# Revit family: EKF_EE_КозырекFORT_PROxima
name_source: partatom
category: Электрооборудование
units: mm (PartAtom-declared; Revit-internal decimal feet)

## family parameters
Всегда вертикально = Нет
На основе рабочей плоскости = Да
Общий = Да
При загрузке вырезать с полостями = Нет
Размер круглого соединителя = Использовать диаметр
Тип детали = Силовой щит
Точка расчета площади = Нет

## types (12) — shared parameters
ADSK_Единица измерения = шт.
ADSK_Завод-изготовитель = EKF
ADSK_Количество = 1
ADSK_Марка = Козырек для FORT
ADSK_Материал = Сталь, с порошковым покрытием, белый
ADSK_Обозначение = Козырек для FORT
ADSK_Размер_Высота = 146 мм
Изготовитель = EKF
Серия номенклатуры = PROxima
Степень защиты IP = -
ТВ = EKF_2
Тип установки = -
zero-valued in all types: ADSK_Масса, Отметка по умолчанию

## per-type parameters (varying)
| type | ADSK_Код изделия | ADSK_Размер_Глубина | ADSK_Размер_Ширина | Тип |
| Козырек для FORT 1000х400 EKF PROxima | FKK104 | 498 мм | 1040 мм | 360 мм |
| Козырек для FORT 1000х600 EKF PROxima | FKK106 | 698 мм | 1040 мм | 361 мм |
| Козырек для FORT 1000х800 EKF PROxima | FKK108 | 898 мм | 1040 мм | 362 мм |
| Козырек для FORT 400х400 EKF PROxima | FKK44 | 498 мм | 440 мм | 363 мм |
| Козырек для FORT 400х600 EKF PROxima | FKK46 | 698 мм | 440 мм | 364 мм |
| Козырек для FORT 400х800 EKF PROxima | FKK48 | 898 мм | 440 мм | 365 мм |
| Козырек для FORT 600х400 EKF PROxima | FKK64 | 498 мм | 640 мм | 366 мм |
| Козырек для FORT 600х600 EKF PROxima | FKK66 | 698 мм | 640 мм | 367 мм |
| Козырек для FORT 600х800 EKF PROxima | FKK68 | 898 мм | 640 мм | 368 мм |
| Козырек для FORT 800х400 EKF PROxima | FKK84 | 498 мм | 840 мм | 369 мм |
| Козырек для FORT 800х600 EKF PROxima | FKK86 | 698 мм | 840 мм | 370 мм |
| Козырек для FORT 800х800 EKF PROxima | FCS86 | 898 мм | 840 мм | 371 мм |

note: column(s) folded — value = type name in every type: ADSK_Наименование
